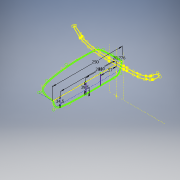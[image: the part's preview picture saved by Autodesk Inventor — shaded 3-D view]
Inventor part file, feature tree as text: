
AUTODESK INVENTOR PART (.ipt)
format: ipt  version: 2019.3 (Build 233278000, 278)  size: 3,230,208 bytes
history: native  units: mm
features: other x16, sketch x3, plane x3, surface_op x3, loft x1
ambient origin geometry x8: Origin, YZ Plane, XZ Plane, XY Plane, X Axis, Y Axis, Z Axis, Center Point
bodies: Body1 (feature_tree), Body2 (feature_tree), Body3 (feature_tree), Body4 (feature_tree)
feature tree (26):
  other  "deck.ipt"
  sketch  "Sketch1"  dims[d15=212.0mm d47=28.0mm]
  sketch  "Sketch2"  dims[d48=145.0mm]
  sketch  "Sketch3"  dims[d107=200.0mm d108=10.0mm d122=84.0mm d130=110.0mm d144=25.0mm d145=25.0mm d150=63.0mm d190=35.5mm d191=38.8mm d192=39.5mm d193=34.5mm d194=110.0mm d195=200.0mm d196=81.0mm d197=25.0mm d199=20.776473mm d316=3.0mm d321=3.0mm d423=140.0mm d425=205.0mm d429=141.0mm d430=250.0mm d455=57.0mm d472=0.0mm d473=90.0deg d474=0.0mm d475=90.0deg d476=0.0mm d477=90.0deg d478=0.0mm d479=90.0deg d488=3.099267mm d489=3.0mm d499=3.0mm]
  other  "Transversal (front)"
  other  "Longitudinal"
  plane  "Work Plane9"
  other  "Transversal (mid)"
  plane  "Work Plane1"
  other  "Transversal (back)"
  plane  "Work Plane7"
  other  "Top"
  other  "Image2"
  other  "Image3"
  other  "Image4"
  other  "Front Profile"
  other  "Srf48"
  other  "Srf49"
  other  "Srf50"
  other  "Edges59"
  other  "Edges60"
  other  "Srf51"
  loft  "LoftSrf13"
  surface_op  "Boundary Patch25"
  surface_op  "Boundary Patch26"
  surface_op  "Boundary Patch27"
